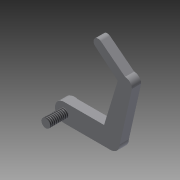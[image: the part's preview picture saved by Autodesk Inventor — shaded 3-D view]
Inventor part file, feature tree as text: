
AUTODESK INVENTOR PART (.ipt)
format: ipt  version: 2015 SP2 (Build 190223200, 223)  size: 115,712 bytes
history: native  units: mm
features: extrude x4, sketch x4, thread x1
ambient origin geometry x8: Origin, YZ Plane, XZ Plane, XY Plane, X Axis, Y Axis, Z Axis, Center Point
bodies: Solid1 (feature_tree)
feature tree (9):
  extrude  "Extrusion1"  Depth=4.0mm
  extrude  "Extrusion2"  Depth=2.0mm TaperAngle=0.0deg
  thread  "Thread1"  [1 undecoded]
  extrude  "Extrusion3"  Depth=0.3mm TaperAngle=0.0deg
  extrude  "Extrusion4"  Depth=2.0mm
  sketch  "Sketch1"  dims[d0=4.0mm d1=1.9mm]
  sketch  "Sketch2"  dims[d2=3.0mm d3=2.0mm d4=0.0mm d5=6.0mm d6=0.5mm d7=0.0mm d8=0.0mm]
  sketch  "Sketch3"  dims[d9=10.0mm d10=0.0mm d11=0.3mm d12=0.0mm]
  sketch  "Sketch4"  dims[d13=2.0mm d14=2.0mm d15=2.0mm d16=0.0mm]
note: 1 required parameter value undecoded (feature->parameter linkage not recoverable at this tier; creation-order binding heuristic only, values carry confidence <= 0.55)
